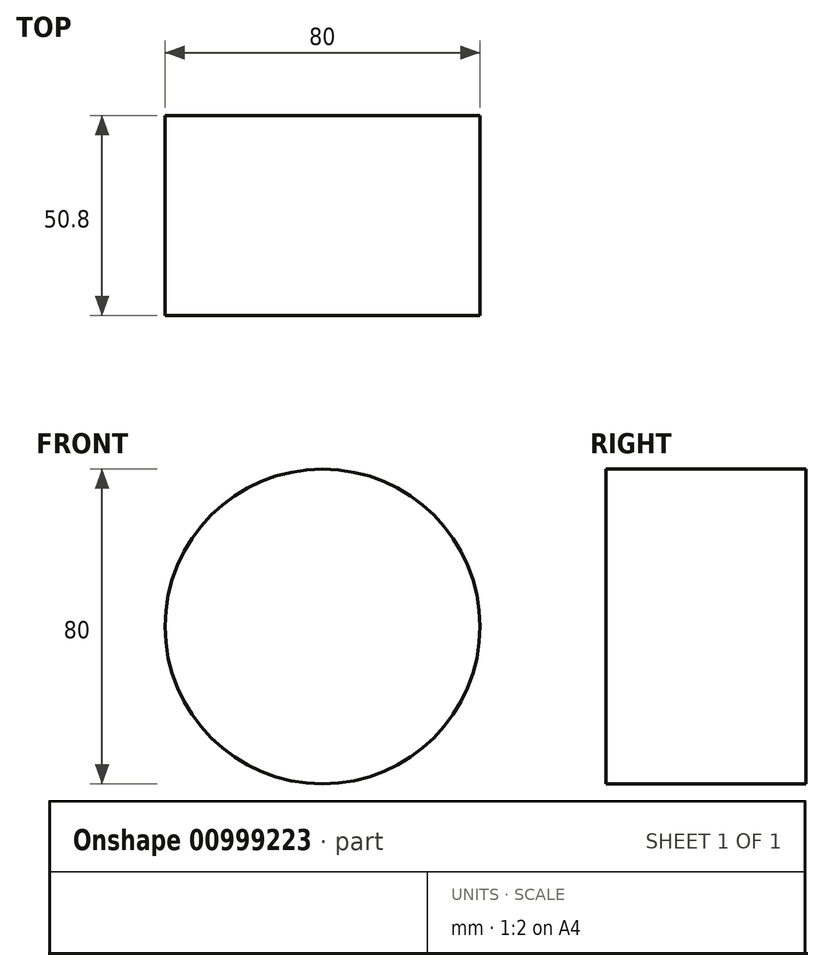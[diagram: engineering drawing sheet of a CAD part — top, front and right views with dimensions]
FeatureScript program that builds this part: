
annotation { "Feature Type Name" : "Feature", "Feature Type Description" : "" }
export const myFeature = defineFeature(function(context is Context, id is Id, definition is map)
    precondition{}
    {
        {
            var Q0;
            Q0=qCreatedBy(makeId("Front.planeOp"),FACE);
            var sketch = newSketch(context, id + "F0", { "sketchPlane" : qUnion([Q0])});
            skCircle(sketch, "E0", {"center": v(0, 0) * mm, "radius": 40 * mm});
            skSolve(sketch);
        }
        {
            var Q0;
            Q0 = qSketchRegion(id + "F0", true);
            extrude(context, id + "F1", {"entities" : qUnion([Q0]), "depth" : 50.8 * mm, "offsetDistance" : 25.4 * mm});
        }
    });
